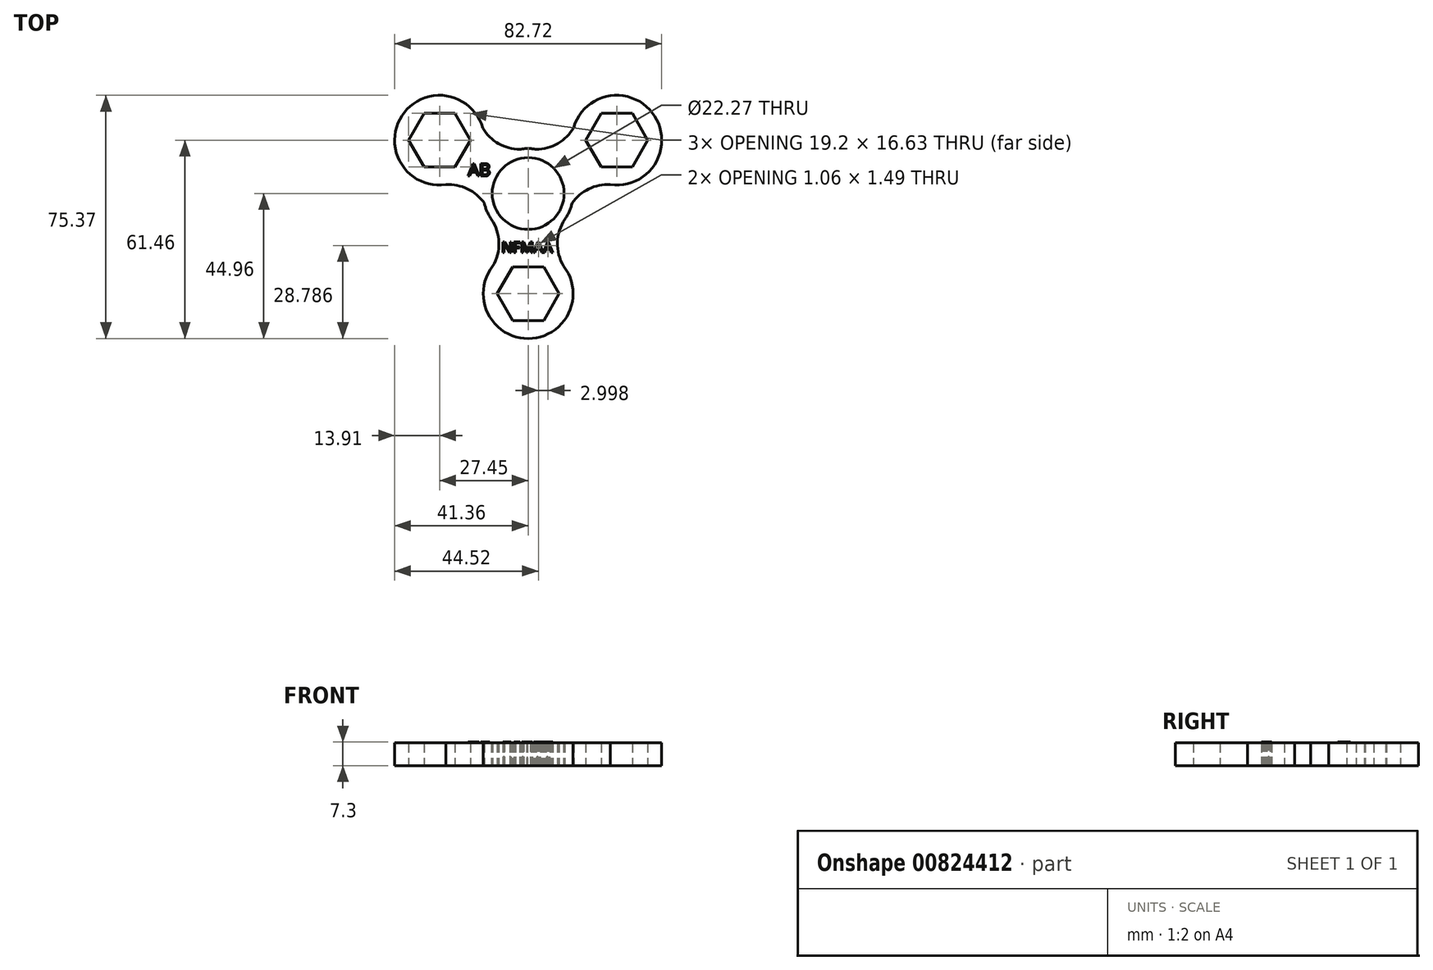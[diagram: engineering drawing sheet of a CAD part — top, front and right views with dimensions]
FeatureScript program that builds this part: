
annotation { "Feature Type Name" : "Feature", "Feature Type Description" : "" }
export const myFeature = defineFeature(function(context is Context, id is Id, definition is map)
    precondition{}
    {
        {
            var Q0;
            Q0=qCreatedBy(makeId("Top.planeOp"),FACE);
            var sketch = newSketch(context, id + "F0", { "sketchPlane" : qUnion([Q0])});
            skCircle(sketch, "E0", {"center": v(0, 0) * mm, "radius": 11.14 * mm});
            skLineSegment(sketch, "E1.0", {"start": v(-17.85, 16.5) * mm, "end": v(-22.65, 8.19) * mm});
            skLineSegment(sketch, "E1.1", {"start": v(-22.65, 8.19) * mm, "end": v(-32.25, 8.19) * mm});
            skLineSegment(sketch, "E1.2", {"start": v(-32.25, 8.19) * mm, "end": v(-37.05, 16.5) * mm});
            skLineSegment(sketch, "E1.3", {"start": v(-37.05, 16.5) * mm, "end": v(-32.25, 24.81) * mm});
            skLineSegment(sketch, "E1.4", {"start": v(-32.25, 24.81) * mm, "end": v(-22.65, 24.81) * mm});
            skLineSegment(sketch, "E1.5", {"start": v(-22.65, 24.81) * mm, "end": v(-17.85, 16.5) * mm});
            skCircle(sketch, "E2", {"center": v(0, 0) * mm, "radius": 13.91 * mm});
            skCircle(sketch, "E3", {"center": v(-27.45, 16.5) * mm, "radius": 13.91 * mm});
            skCircle(sketch, "E4.MirrorC", {"center": v(27.45, 16.5) * mm, "radius": 13.91 * mm});
            skLineSegment(sketch, "E5.0", {"start": v(9.6, -31.04) * mm, "end": v(4.8, -39.36) * mm});
            skLineSegment(sketch, "E5.1", {"start": v(4.8, -39.36) * mm, "end": v(-4.8, -39.36) * mm});
            skLineSegment(sketch, "E5.2", {"start": v(-4.8, -39.36) * mm, "end": v(-9.6, -31.04) * mm});
            skLineSegment(sketch, "E5.3", {"start": v(-9.6, -31.04) * mm, "end": v(-4.8, -22.73) * mm});
            skLineSegment(sketch, "E5.4", {"start": v(-4.8, -22.73) * mm, "end": v(4.8, -22.73) * mm});
            skLineSegment(sketch, "E5.5", {"start": v(4.8, -22.73) * mm, "end": v(9.6, -31.04) * mm});
            skCircle(sketch, "E6", {"center": v(0, -31.04) * mm, "radius": 13.91 * mm});
            skLineSegment(sketch, "E7.MirrorCS", {"start": v(22.65, 24.81) * mm, "end": v(17.85, 16.5) * mm});
            skLineSegment(sketch, "E8.MirrorCS", {"start": v(32.25, 24.81) * mm, "end": v(22.65, 24.81) * mm});
            skLineSegment(sketch, "E9.MirrorCS", {"start": v(37.05, 16.5) * mm, "end": v(32.25, 24.81) * mm});
            skLineSegment(sketch, "E10.MirrorCS", {"start": v(32.25, 8.19) * mm, "end": v(37.05, 16.5) * mm});
            skLineSegment(sketch, "E11.MirrorCS", {"start": v(22.65, 8.19) * mm, "end": v(32.25, 8.19) * mm});
            skLineSegment(sketch, "E12.MirrorCS", {"start": v(17.85, 16.5) * mm, "end": v(22.65, 8.19) * mm});
            skArc(sketch, "E13", {"start": v(-15.45, 23.54) * mm, "mid": v(-9.6, 15.7) * mm, "end": v(0, 13.91) * mm});
            skArc(sketch, "E14", {"start": v(0, 13.91) * mm, "mid": v(9.47, 15.67) * mm, "end": v(15.32, 23.32) * mm});
            skArc(sketch, "E15", {"start": v(-11.48, -7.86) * mm, "mid": v(-16.94, 0.36) * mm, "end": v(-26.55, 2.61) * mm});
            skArc(sketch, "E16.MirrorCS", {"start": v(11.48, -7.86) * mm, "mid": v(16.94, 0.36) * mm, "end": v(26.55, 2.61) * mm});
            skArc(sketch, "E17", {"start": v(11.48, -7.86) * mm, "mid": v(9.06, -15.88) * mm, "end": v(11.86, -23.77) * mm});
            skArc(sketch, "E18.MirrorCS", {"start": v(-11.48, -7.86) * mm, "mid": v(-9.06, -15.88) * mm, "end": v(-11.86, -23.77) * mm});
            skSolve(sketch);
        }
        {
            var Q0;
            Q0=qCreatedBy(makeId("Top.planeOp"),FACE);
            var sketch = newSketch(context, id + "F1", { "sketchPlane" : qUnion([Q0])});
            skText(sketch, "E19", { "text": "NFMAA", "fontName": "OpenSans-Regular.ttf"});
            const initialGuessF1  = {"E19": [-0.00825, -0.0183, 1, 0, 0.0033]};
            skSetInitialGuess(sketch, initialGuessF1);
            skSolve(sketch);
        }
        {
            var Q0;
            Q0 = qSketchRegion(id + "F1", true);
            extrude(context, id + "F2", {"entities" : qUnion([Q0]), "depth" : 7.3 * mm, "offsetDistance" : 25 * mm});
        }
        {
            var Q0;
            Q0 = qSketchRegion(id + "F0", true);
            extrude(context, id + "F3", {"entities" : qUnion([Q0]), "depth" : 7 * mm, "offsetDistance" : 25 * mm});
        }
        {
            var Q0;
            Q0=qCreatedBy(makeId("Top.planeOp"),FACE);
            var sketch = newSketch(context, id + "F4", { "sketchPlane" : qUnion([Q0])});
            skText(sketch, "E20", { "text": "AB", "fontName": "OpenSans-Regular.ttf"});
            const initialGuessF4  = {"E20": [-0.0186, 0.0054, 1, 0, 0.0039]};
            skSetInitialGuess(sketch, initialGuessF4);
            skSolve(sketch);
        }
        {
            var Q0;
            Q0 = qSketchRegion(id + "F4", true);
            extrude(context, id + "F5", {"entities" : qUnion([Q0]), "operationType" : NewBodyOperationType.ADD, "depth" : 7.3 * mm, "offsetDistance" : 25 * mm});
        }
    });
